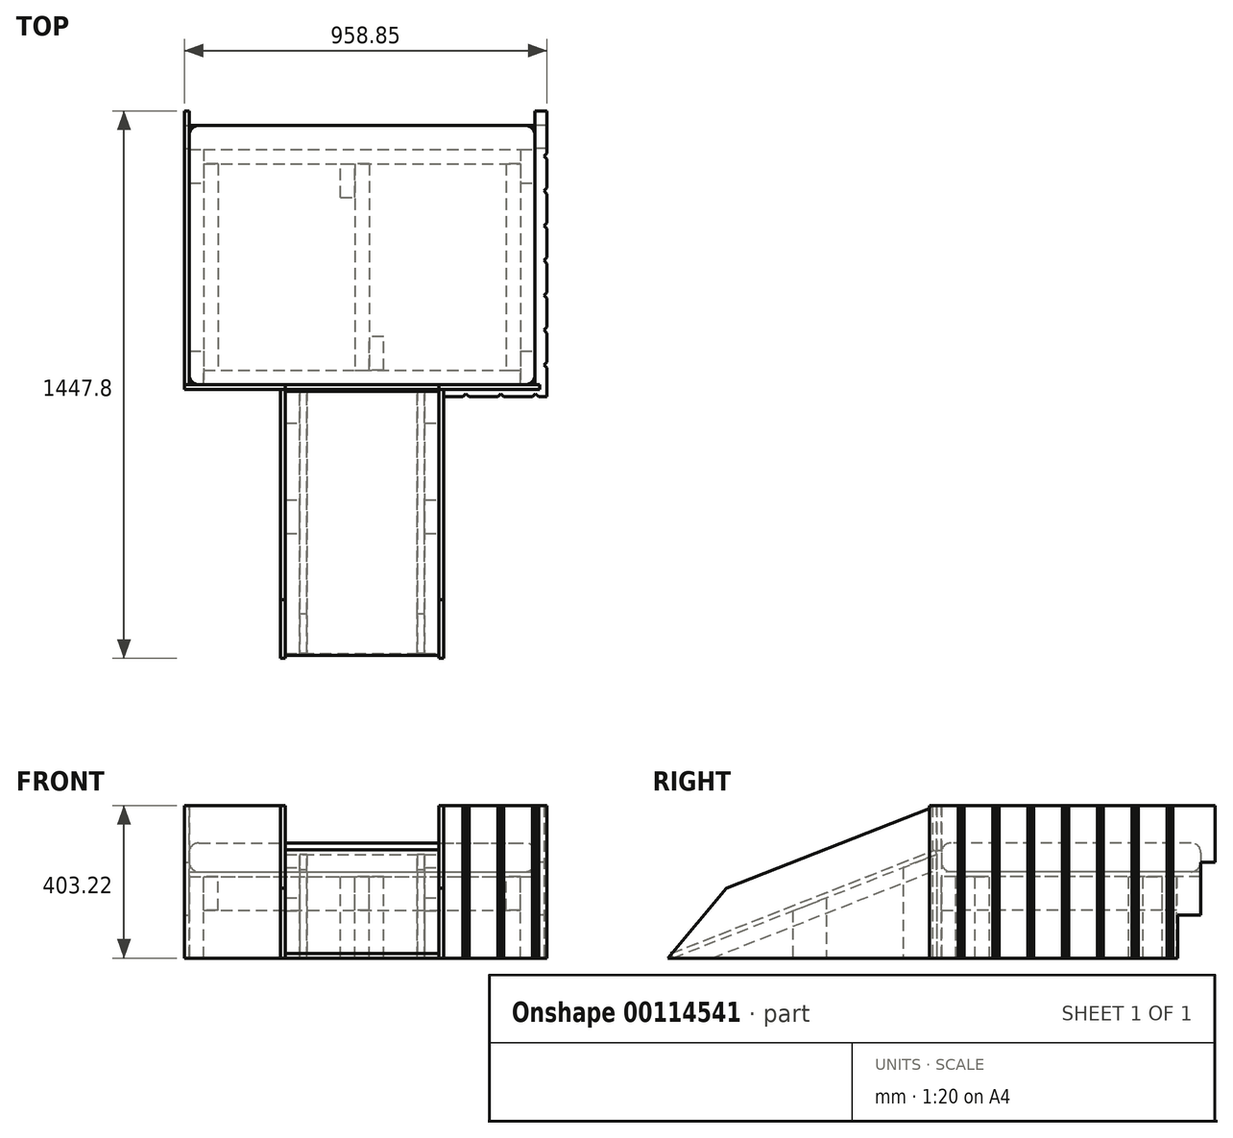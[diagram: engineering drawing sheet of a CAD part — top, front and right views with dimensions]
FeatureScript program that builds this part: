
annotation { "Feature Type Name" : "Feature", "Feature Type Description" : "" }
export const myFeature = defineFeature(function(context is Context, id is Id, definition is map)
    precondition{}
    {
        {
            var Q0;
            Q0=qCreatedBy(makeId("Top.planeOp"),FACE);
            var sketch = newSketch(context, id + "F0", { "sketchPlane" : qUnion([Q0])});
            skLineSegment(sketch, "E0.bottom", {"start": v(-457.2, 0) * mm, "end": v(457.2, 0) * mm});
            skLineSegment(sketch, "E0.top", {"start": v(-457.2, -685.8) * mm, "end": v(457.2, -685.8) * mm});
            skLineSegment(sketch, "E0.left", {"start": v(-457.2, 0) * mm, "end": v(-457.2, -685.8) * mm});
            skLineSegment(sketch, "E0.right", {"start": v(457.2, 0) * mm, "end": v(457.2, -685.8) * mm});
            skLineSegment(sketch, "E1", {"start": v(0, 0) * mm, "end": v(0, -685.8) * mm, "construction": true});
            skSolve(sketch);
        }
        {
            var Q0;
            Q0 = qSketchRegion(id + "F0", true);
            extrude(context, id + "F1", {"entities" : qUnion([Q0]), "oppositeDirection" : true, "depth" : 12.7 * mm});
        }
        {
            var Q0;
            Q0=makeQuery(id+"F1.opExtrude","CAP_FACE",FACE,{"disambiguationData":[OSD([sQuery(id+"F0.wireOp",EDGE,"E0.bottom"),sQuery(id+"F0.wireOp",EDGE,"E0.top"),sQuery(id+"F0.wireOp",EDGE,"E0.left"),sQuery(id+"F0.wireOp",EDGE,"E0.right")])],"isStart":false});
            var sketch = newSketch(context, id + "F2", { "sketchPlane" : qUnion([Q0])});
            skLineSegment(sketch, "E2.bottom", {"start": v(-457.2, 63.5) * mm, "end": v(-419.1, 63.5) * mm});
            skLineSegment(sketch, "E2.top", {"start": v(-457.2, 152.4) * mm, "end": v(-419.1, 152.4) * mm});
            skLineSegment(sketch, "E2.left", {"start": v(-457.2, 63.5) * mm, "end": v(-457.2, 152.4) * mm});
            skLineSegment(sketch, "E2.right", {"start": v(-419.1, 63.5) * mm, "end": v(-419.1, 152.4) * mm});
            skLineSegment(sketch, "E3.bottom", {"start": v(-457.2, 596.9) * mm, "end": v(-419.1, 596.9) * mm});
            skLineSegment(sketch, "E3.top", {"start": v(-457.2, 685.8) * mm, "end": v(-419.1, 685.8) * mm});
            skLineSegment(sketch, "E3.left", {"start": v(-457.2, 596.9) * mm, "end": v(-457.2, 685.8) * mm});
            skLineSegment(sketch, "E3.right", {"start": v(-419.1, 596.9) * mm, "end": v(-419.1, 685.8) * mm});
            skLineSegment(sketch, "E4.bottom", {"start": v(419.1, 63.5) * mm, "end": v(457.2, 63.5) * mm});
            skLineSegment(sketch, "E4.top", {"start": v(419.1, 152.4) * mm, "end": v(457.2, 152.4) * mm});
            skLineSegment(sketch, "E4.left", {"start": v(419.1, 63.5) * mm, "end": v(419.1, 152.4) * mm});
            skLineSegment(sketch, "E4.right", {"start": v(457.2, 63.5) * mm, "end": v(457.2, 152.4) * mm});
            skLineSegment(sketch, "E5.bottom", {"start": v(419.1, 596.9) * mm, "end": v(457.2, 596.9) * mm});
            skLineSegment(sketch, "E5.top", {"start": v(419.1, 685.8) * mm, "end": v(457.2, 685.8) * mm});
            skLineSegment(sketch, "E5.left", {"start": v(419.1, 596.9) * mm, "end": v(419.1, 685.8) * mm});
            skLineSegment(sketch, "E5.right", {"start": v(457.2, 596.9) * mm, "end": v(457.2, 685.8) * mm});
            skLineSegment(sketch, "E6.bottom", {"start": v(-57.15, 190.5) * mm, "end": v(-19.05, 190.5) * mm});
            skLineSegment(sketch, "E6.top", {"start": v(-57.15, 101.6) * mm, "end": v(-19.05, 101.6) * mm});
            skLineSegment(sketch, "E6.left", {"start": v(-57.15, 190.5) * mm, "end": v(-57.15, 101.6) * mm});
            skLineSegment(sketch, "E6.right", {"start": v(-19.05, 190.5) * mm, "end": v(-19.05, 101.6) * mm});
            skLineSegment(sketch, "E7.bottom", {"start": v(57.15, 647.7) * mm, "end": v(19.05, 647.7) * mm});
            skLineSegment(sketch, "E7.top", {"start": v(57.15, 558.8) * mm, "end": v(19.05, 558.8) * mm});
            skLineSegment(sketch, "E7.left", {"start": v(57.15, 647.7) * mm, "end": v(57.15, 558.8) * mm});
            skLineSegment(sketch, "E7.right", {"start": v(19.05, 647.7) * mm, "end": v(19.05, 558.8) * mm});
            skSolve(sketch);
        }
        {
            var Q0;
            Q0 = qSketchRegion(id + "F2", true);
            extrude(context, id + "F3", {"entities" : qUnion([Q0]), "operationType" : NewBodyOperationType.ADD, "depth" : 215.9 * mm});
        }
        {
            var Q0;
            Q0=makeQuery(id+"F3.opExtrude","CAP_FACE",FACE,{"disambiguationData":[OSD([sQuery(id+"F2.wireOp",EDGE,"E5.bottom"),sQuery(id+"F2.wireOp",EDGE,"E5.top"),sQuery(id+"F2.wireOp",EDGE,"E5.left"),sQuery(id+"F2.wireOp",EDGE,"E5.right")])],"isStart":false});
            var sketch = newSketch(context, id + "F4", { "sketchPlane" : qUnion([Q0])});
            skLineSegment(sketch, "E8.bottom", {"start": v(203.2, 698.5) * mm, "end": v(165.1, 698.5) * mm});
            skLineSegment(sketch, "E8.top", {"start": v(203.2, 787.4) * mm, "end": v(165.1, 787.4) * mm});
            skLineSegment(sketch, "E8.left", {"start": v(203.2, 698.5) * mm, "end": v(203.2, 787.4) * mm});
            skLineSegment(sketch, "E8.right", {"start": v(165.1, 698.5) * mm, "end": v(165.1, 787.4) * mm});
            skLineSegment(sketch, "E9.bottom", {"start": v(-165.1, 698.5) * mm, "end": v(-203.2, 698.5) * mm});
            skLineSegment(sketch, "E9.top", {"start": v(-165.1, 787.4) * mm, "end": v(-203.2, 787.4) * mm});
            skLineSegment(sketch, "E9.left", {"start": v(-165.1, 698.5) * mm, "end": v(-165.1, 787.4) * mm});
            skLineSegment(sketch, "E9.right", {"start": v(-203.2, 698.5) * mm, "end": v(-203.2, 787.4) * mm});
            skLineSegment(sketch, "E10.bottom", {"start": v(203.2, 990.6) * mm, "end": v(165.1, 990.6) * mm});
            skLineSegment(sketch, "E10.top", {"start": v(203.2, 1079.5) * mm, "end": v(165.1, 1079.5) * mm});
            skLineSegment(sketch, "E10.left", {"start": v(203.2, 990.6) * mm, "end": v(203.2, 1079.5) * mm});
            skLineSegment(sketch, "E10.right", {"start": v(165.1, 990.6) * mm, "end": v(165.1, 1079.5) * mm});
            skLineSegment(sketch, "E11.bottom", {"start": v(-165.1, 990.6) * mm, "end": v(-203.2, 990.6) * mm});
            skLineSegment(sketch, "E11.top", {"start": v(-165.1, 1079.5) * mm, "end": v(-203.2, 1079.5) * mm});
            skLineSegment(sketch, "E11.left", {"start": v(-165.1, 990.6) * mm, "end": v(-165.1, 1079.5) * mm});
            skLineSegment(sketch, "E11.right", {"start": v(-203.2, 990.6) * mm, "end": v(-203.2, 1079.5) * mm});
            skSolve(sketch);
        }
        {
            var Q0;
            Q0 = qSketchRegion(id + "F4", true);
            extrude(context, id + "F5", {"entities" : qUnion([Q0]), "operationType" : NewBodyOperationType.ADD, "oppositeDirection" : true, "depth" : 279.4 * mm});
        }
        {
            var Q0;
            Q0=makeQuery(id+"F5.opExtrude","SWEPT_FACE",FACE,{"disambiguationData":[OSD([sQuery(id+"F4.wireOp",EDGE,"E9.right")])]});
            var sketch = newSketch(context, id + "F6", { "sketchPlane" : qUnion([Q0])});
            skLineSegment(sketch, "E12", {"start": v(685.8, 50.8) * mm, "end": v(1397, -228.6) * mm});
            skLineSegment(sketch, "E13", {"start": v(1397, -228.6) * mm, "end": v(1397, 149.23) * mm});
            skLineSegment(sketch, "E14", {"start": v(1397, 149.23) * mm, "end": v(685.8, 149.23) * mm});
            skLineSegment(sketch, "E15", {"start": v(685.8, 149.23) * mm, "end": v(685.8, 50.8) * mm});
            skSolve(sketch);
        }
        {
            var Q0;
            Q0 = qSketchRegion(id + "F6", true);
            extrude(context, id + "F7", {"entities" : qUnion([Q0]), "operationType" : NewBodyOperationType.REMOVE, "oppositeDirection" : true, "depth" : 914.4 * mm});
        }
        {
            var Q0;
            Q0=makeQuery(id+"F7.boolean.opBoolean","COPY",FACE,{"disambiguationData":[OD(3.0)],"derivedFrom":makeQuery(id+"F7.opExtrude","SWEPT_FACE",FACE,{"disambiguationData":[OSD([sQuery(id+"F6.wireOp",EDGE,"E12")])]})});
            var sketch = newSketch(context, id + "F8", { "sketchPlane" : qUnion([Q0])});
            skLineSegment(sketch, "E16.bottom", {"start": v(-203.2, -1383.85) * mm, "end": v(203.2, -1383.85) * mm});
            skLineSegment(sketch, "E16.top", {"start": v(-203.2, -633.38) * mm, "end": v(203.2, -633.38) * mm});
            skLineSegment(sketch, "E16.left", {"start": v(-203.2, -1383.85) * mm, "end": v(-203.2, -633.38) * mm});
            skLineSegment(sketch, "E16.right", {"start": v(203.2, -1383.85) * mm, "end": v(203.2, -633.38) * mm});
            skSolve(sketch);
        }
        {
            var Q0;
            Q0 = qSketchRegion(id + "F8", true);
            extrude(context, id + "F9", {"entities" : qUnion([Q0]), "depth" : 12.7 * mm});
        }
        {
            var Q0;
            Q0=makeQuery(id+"F3.boolean.opBoolean","MERGE",FACE,{"derivedFrom":[makeQuery(id+"F1.opExtrude","SWEPT_FACE",FACE,{"disambiguationData":[OSD([sQuery(id+"F0.wireOp",EDGE,"E0.top")])]}),makeQuery(id+"F3.opExtrude","SWEPT_FACE",FACE,{"disambiguationData":[OSD([sQuery(id+"F2.wireOp",EDGE,"E3.top")])]}),makeQuery(id+"F3.opExtrude","SWEPT_FACE",FACE,{"disambiguationData":[OSD([sQuery(id+"F2.wireOp",EDGE,"E5.top")])]})]});
            var sketch = newSketch(context, id + "F10", { "sketchPlane" : qUnion([Q0])});
            skLineSegment(sketch, "E17", {"start": v(469.9, -228.6) * mm, "end": v(-469.9, -228.6) * mm});
            skLineSegment(sketch, "E18", {"start": v(-469.9, -228.6) * mm, "end": v(-469.9, 174.62) * mm});
            skLineSegment(sketch, "E19", {"start": v(-469.9, 174.62) * mm, "end": v(-203.2, 174.62) * mm});
            skLineSegment(sketch, "E20", {"start": v(-203.2, 174.62) * mm, "end": v(-203.2, 57.15) * mm});
            skLineSegment(sketch, "E21", {"start": v(-203.2, 57.15) * mm, "end": v(203.2, 57.15) * mm});
            skLineSegment(sketch, "E22", {"start": v(203.2, 57.15) * mm, "end": v(203.2, 174.63) * mm});
            skLineSegment(sketch, "E23", {"start": v(203.2, 174.63) * mm, "end": v(469.9, 174.63) * mm});
            skLineSegment(sketch, "E24", {"start": v(469.9, 174.63) * mm, "end": v(469.9, -228.6) * mm});
            skSolve(sketch);
        }
        {
            var Q0;
            Q0 = qSketchRegion(id + "F10", true);
            extrude(context, id + "F11", {"entities" : qUnion([Q0]), "depth" : 12.7 * mm});
        }
        {
            var Q0;
            Q0=makeQuery(id+"F3.boolean.opBoolean","MERGE",FACE,{"derivedFrom":[makeQuery(id+"F1.opExtrude","SWEPT_FACE",FACE,{"disambiguationData":[OSD([sQuery(id+"F0.wireOp",EDGE,"E0.right")])]}),makeQuery(id+"F3.opExtrude","SWEPT_FACE",FACE,{"disambiguationData":[OSD([sQuery(id+"F2.wireOp",EDGE,"E4.right")])]}),makeQuery(id+"F3.opExtrude","SWEPT_FACE",FACE,{"disambiguationData":[OSD([sQuery(id+"F2.wireOp",EDGE,"E5.right")])]})]});
            var sketch = newSketch(context, id + "F12", { "sketchPlane" : qUnion([Q0])});
            skLineSegment(sketch, "E25", {"start": v(-685.8, -228.6) * mm, "end": v(-685.8, 174.62) * mm});
            skLineSegment(sketch, "E26", {"start": v(-685.8, 174.63) * mm, "end": v(38.1, 174.63) * mm});
            skLineSegment(sketch, "E27", {"start": v(-60.32, -228.6) * mm, "end": v(-685.8, -228.6) * mm});
            skLineSegment(sketch, "E28", {"start": v(38.1, 174.63) * mm, "end": v(38.1, 25.4) * mm});
            skLineSegment(sketch, "E29", {"start": v(38.1, 25.4) * mm, "end": v(0, 25.4) * mm});
            skLineSegment(sketch, "E30", {"start": v(0, 25.4) * mm, "end": v(0, -114.3) * mm});
            skLineSegment(sketch, "E31", {"start": v(0, -114.3) * mm, "end": v(-60.32, -114.3) * mm});
            skLineSegment(sketch, "E32", {"start": v(-60.32, -228.6) * mm, "end": v(-60.32, -114.3) * mm});
            skSolve(sketch);
        }
        {
            var Q0;
            Q0 = qSketchRegion(id + "F12", true);
            extrude(context, id + "F13", {"entities" : qUnion([Q0]), "depth" : 12.7 * mm});
        }
        {
            var Q0;
            Q0=makeQuery(id+"F3.boolean.opBoolean","MERGE",FACE,{"derivedFrom":[makeQuery(id+"F1.opExtrude","SWEPT_FACE",FACE,{"disambiguationData":[OSD([sQuery(id+"F0.wireOp",EDGE,"E0.left")])]}),makeQuery(id+"F3.opExtrude","SWEPT_FACE",FACE,{"disambiguationData":[OSD([sQuery(id+"F2.wireOp",EDGE,"E2.left")])]}),makeQuery(id+"F3.opExtrude","SWEPT_FACE",FACE,{"disambiguationData":[OSD([sQuery(id+"F2.wireOp",EDGE,"E3.left")])]})]});
            var sketch = newSketch(context, id + "F14", { "sketchPlane" : qUnion([Q0])});
            skLineSegment(sketch, "E33", {"start": v(685.8, -228.6) * mm, "end": v(60.32, -228.6) * mm});
            skLineSegment(sketch, "E34", {"start": v(-38.1, 174.62) * mm, "end": v(685.8, 174.63) * mm});
            skLineSegment(sketch, "E35", {"start": v(685.8, 174.63) * mm, "end": v(685.8, -228.6) * mm});
            skLineSegment(sketch, "E36", {"start": v(60.32, -228.6) * mm, "end": v(60.32, -114.3) * mm});
            skLineSegment(sketch, "E37", {"start": v(60.32, -114.3) * mm, "end": v(0, -114.3) * mm});
            skLineSegment(sketch, "E38", {"start": v(0, -114.3) * mm, "end": v(0, 25.4) * mm});
            skLineSegment(sketch, "E39", {"start": v(0, 25.4) * mm, "end": v(-38.1, 25.4) * mm});
            skLineSegment(sketch, "E40", {"start": v(-38.1, 25.4) * mm, "end": v(-38.1, 174.62) * mm});
            skSolve(sketch);
        }
        {
            var Q0;
            Q0 = qSketchRegion(id + "F14", true);
            extrude(context, id + "F15", {"entities" : qUnion([Q0]), "depth" : 12.7 * mm});
        }
        {
            var Q0;
            Q0=makeQuery(id+"F5.opExtrude","SWEPT_FACE",FACE,{"disambiguationData":[OSD([sQuery(id+"F4.wireOp",EDGE,"E8.left")])]});
            var sketch = newSketch(context, id + "F16", { "sketchPlane" : qUnion([Q0])});
            skLineSegment(sketch, "E41", {"start": v(-698.5, -228.6) * mm, "end": v(-698.5, 174.63) * mm});
            skLineSegment(sketch, "E42", {"start": v(-698.5, 174.63) * mm, "end": v(-1254.7, -43.88) * mm});
            skLineSegment(sketch, "E43", {"start": v(-1409.7, -228.6) * mm, "end": v(-698.5, -228.6) * mm});
            skLineSegment(sketch, "E44", {"start": v(-1409.7, -228.6) * mm, "end": v(-1254.7, -43.88) * mm});
            skSolve(sketch);
        }
        {
            var Q0;
            Q0 = qSketchRegion(id + "F16", true);
            extrude(context, id + "F17", {"entities" : qUnion([Q0]), "depth" : 12.7 * mm});
        }
        {
            var Q0;
            Q0=makeQuery(id+"F3.opExtrude","SWEPT_FACE",FACE,{"disambiguationData":[OSD([sQuery(id+"F2.wireOp",EDGE,"E5.left")])]});
            var sketch = newSketch(context, id + "F18", { "sketchPlane" : qUnion([Q0])});
            skLineSegment(sketch, "E45.bottom", {"start": v(685.8, -12.7) * mm, "end": v(647.7, -12.7) * mm});
            skLineSegment(sketch, "E45.top", {"start": v(685.8, -101.6) * mm, "end": v(647.7, -101.6) * mm});
            skLineSegment(sketch, "E45.left", {"start": v(685.8, -12.7) * mm, "end": v(685.8, -101.6) * mm});
            skLineSegment(sketch, "E45.right", {"start": v(647.7, -12.7) * mm, "end": v(647.7, -101.6) * mm});
            skLineSegment(sketch, "E46.bottom", {"start": v(63.5, -12.7) * mm, "end": v(101.6, -12.7) * mm});
            skLineSegment(sketch, "E46.top", {"start": v(63.5, -101.6) * mm, "end": v(101.6, -101.6) * mm});
            skLineSegment(sketch, "E46.left", {"start": v(63.5, -12.7) * mm, "end": v(63.5, -101.6) * mm});
            skLineSegment(sketch, "E46.right", {"start": v(101.6, -12.7) * mm, "end": v(101.6, -101.6) * mm});
            skSolve(sketch);
        }
        {
            var Q0;
            Q0 = qSketchRegion(id + "F18", true);
            extrude(context, id + "F19", {"entities" : qUnion([Q0]), "depth" : 838.2 * mm});
        }
        {
            var Q0;
            Q0=makeQuery(id+"F19.opExtrude","SWEPT_FACE",FACE,{"disambiguationData":[OSD([sQuery(id+"F18.wireOp",EDGE,"E45.right")])]});
            var sketch = newSketch(context, id + "F20", { "sketchPlane" : qUnion([Q0])});
            skLineSegment(sketch, "E47.bottom", {"start": v(-19.05, -12.7) * mm, "end": v(19.05, -12.7) * mm});
            skLineSegment(sketch, "E47.top", {"start": v(-19.05, -101.6) * mm, "end": v(19.05, -101.6) * mm});
            skLineSegment(sketch, "E47.left", {"start": v(-19.05, -12.7) * mm, "end": v(-19.05, -101.6) * mm});
            skLineSegment(sketch, "E47.right", {"start": v(19.05, -12.7) * mm, "end": v(19.05, -101.6) * mm});
            skLineSegment(sketch, "E48.bottom", {"start": v(-419.1, -12.7) * mm, "end": v(-381, -12.7) * mm});
            skLineSegment(sketch, "E48.top", {"start": v(-419.1, -101.6) * mm, "end": v(-381, -101.6) * mm});
            skLineSegment(sketch, "E48.left", {"start": v(-419.1, -12.7) * mm, "end": v(-419.1, -101.6) * mm});
            skLineSegment(sketch, "E48.right", {"start": v(-381, -12.7) * mm, "end": v(-381, -101.6) * mm});
            skLineSegment(sketch, "E49.bottom", {"start": v(419.1, -12.7) * mm, "end": v(381, -12.7) * mm});
            skLineSegment(sketch, "E49.top", {"start": v(419.1, -101.6) * mm, "end": v(381, -101.6) * mm});
            skLineSegment(sketch, "E49.left", {"start": v(419.1, -12.7) * mm, "end": v(419.1, -101.6) * mm});
            skLineSegment(sketch, "E49.right", {"start": v(381, -12.7) * mm, "end": v(381, -101.6) * mm});
            skSolve(sketch);
        }
        {
            var Q0;
            Q0 = qSketchRegion(id + "F20", true);
            extrude(context, id + "F21", {"entities" : qUnion([Q0]), "endBound" : BoundingType.UP_TO_NEXT, "depth" : 25.4 * mm});
        }
        {
            var Q0;
            Q0=makeQuery(id+"F17.opExtrude","SWEPT_BODY",BODY,{"disambiguationData":[OSD([sQuery(id+"F16.wireOp",EDGE,"E41"),sQuery(id+"F16.wireOp",EDGE,"fiiTlYLV-duia-QpJI-SALt-FYDScrY8uBnS"),sQuery(id+"F16.wireOp",EDGE,"e7RRUxPj-3naJ-ncjy-4rKp-VtwRg2sKKchD"),sQuery(id+"F16.wireOp",EDGE,"E42"),sQuery(id+"F16.wireOp",EDGE,"E43"),sQuery(id+"F16.wireOp",EDGE,"E44")])]});
            transform(context, id + "F22", {"entities" : qUnion([Q0]), "transformType" : TransformType.TRANSLATION_3D, "dx" : -419.1 * mm, "dy" : 0 * mm, "dz" : 0 * mm, "makeCopy" : true});
        }
        {
            var Q0;
            Q0=makeQuery(id+"F5.opExtrude","SWEPT_FACE",FACE,{"disambiguationData":[OSD([sQuery(id+"F4.wireOp",EDGE,"E11.left")])]});
            var sketch = newSketch(context, id + "F23", { "sketchPlane" : qUnion([Q0])});
            skLineSegment(sketch, "E50", {"start": v(-698.5, 45.81) * mm, "end": v(-1397, -228.6) * mm});
            skLineSegment(sketch, "E51", {"start": v(-1397, -228.6) * mm, "end": v(-1292.8, -228.6) * mm});
            skLineSegment(sketch, "E52", {"start": v(-1292.8, -228.6) * mm, "end": v(-698.5, 4.88) * mm});
            skLineSegment(sketch, "E53", {"start": v(-698.5, 4.88) * mm, "end": v(-698.5, 45.81) * mm});
            skSolve(sketch);
        }
        {
            var Q0;
            Q0 = qSketchRegion(id + "F23", true);
            extrude(context, id + "F24", {"entities" : qUnion([Q0]), "depth" : 19.05 * mm});
        }
        {
            var Q0;
            Q0=makeQuery(id+"F24.opExtrude","SWEPT_BODY",BODY,{"disambiguationData":[OSD([sQuery(id+"F23.wireOp",EDGE,"E50"),sQuery(id+"F23.wireOp",EDGE,"E51"),sQuery(id+"F23.wireOp",EDGE,"E52"),sQuery(id+"F23.wireOp",EDGE,"E53")])]});
            transform(context, id + "F25", {"entities" : qUnion([Q0]), "transformType" : TransformType.TRANSLATION_3D, "dx" : 311.15 * mm, "dy" : 0 * mm, "dz" : 0 * mm, "makeCopy" : true});
        }
        {
            var Q0;
            Q0=makeQuery(id+"F11.opExtrude","SWEPT_FACE",FACE,{"disambiguationData":[OSD([sQuery(id+"F10.wireOp",EDGE,"E17")])]});
            var sketch = newSketch(context, id + "F26", { "sketchPlane" : qUnion([Q0])});
            skLineSegment(sketch, "E54", {"start": v(215.9, 698.5) * mm, "end": v(215.9, 717.55) * mm});
            skLineSegment(sketch, "E55", {"start": v(215.9, 717.55) * mm, "end": v(266.7, 717.55) * mm});
            skLineSegment(sketch, "E56", {"start": v(266.7, 717.55) * mm, "end": v(274.64, 709.61) * mm});
            skLineSegment(sketch, "E57", {"start": v(274.64, 709.61) * mm, "end": v(282.57, 717.55) * mm});
            skLineSegment(sketch, "E58", {"start": v(282.57, 717.55) * mm, "end": v(358.77, 717.55) * mm});
            skLineSegment(sketch, "E59", {"start": v(358.77, 717.55) * mm, "end": v(366.71, 709.61) * mm});
            skLineSegment(sketch, "E60", {"start": v(366.71, 709.61) * mm, "end": v(374.65, 717.55) * mm});
            skLineSegment(sketch, "E61", {"start": v(374.65, 717.55) * mm, "end": v(450.85, 717.55) * mm});
            skLineSegment(sketch, "E62", {"start": v(450.85, 717.55) * mm, "end": v(458.79, 709.61) * mm});
            skLineSegment(sketch, "E63", {"start": v(458.79, 709.61) * mm, "end": v(466.72, 717.55) * mm});
            skLineSegment(sketch, "E64", {"start": v(466.72, 717.55) * mm, "end": v(488.95, 717.55) * mm});
            skLineSegment(sketch, "E65", {"start": v(488.95, 717.55) * mm, "end": v(488.95, 641.35) * mm});
            skLineSegment(sketch, "E66", {"start": v(488.95, 641.35) * mm, "end": v(481.01, 633.41) * mm});
            skLineSegment(sketch, "E67", {"start": v(481.01, 633.41) * mm, "end": v(488.95, 625.48) * mm});
            skLineSegment(sketch, "E68", {"start": v(488.95, 625.48) * mm, "end": v(488.95, 549.28) * mm});
            skLineSegment(sketch, "E69", {"start": v(488.95, 549.28) * mm, "end": v(481.01, 541.34) * mm});
            skLineSegment(sketch, "E70", {"start": v(481.01, 541.34) * mm, "end": v(488.95, 533.4) * mm});
            skLineSegment(sketch, "E71", {"start": v(488.95, 533.4) * mm, "end": v(488.95, 457.2) * mm});
            skLineSegment(sketch, "E72", {"start": v(488.95, 457.2) * mm, "end": v(481.01, 449.26) * mm});
            skLineSegment(sketch, "E73", {"start": v(481.01, 449.26) * mm, "end": v(488.95, 441.33) * mm});
            skLineSegment(sketch, "E74", {"start": v(488.95, 441.33) * mm, "end": v(488.95, 365.13) * mm});
            skLineSegment(sketch, "E75", {"start": v(488.95, 365.13) * mm, "end": v(481.01, 357.19) * mm});
            skLineSegment(sketch, "E76", {"start": v(481.01, 357.19) * mm, "end": v(488.95, 349.25) * mm});
            skLineSegment(sketch, "E77", {"start": v(488.95, 349.25) * mm, "end": v(488.95, 273.05) * mm});
            skLineSegment(sketch, "E78", {"start": v(469.9, 698.5) * mm, "end": v(215.9, 698.5) * mm});
            skLineSegment(sketch, "E79", {"start": v(469.9, 698.5) * mm, "end": v(469.9, 60.32) * mm});
            skLineSegment(sketch, "E80", {"start": v(469.9, 60.32) * mm, "end": v(488.95, 60.32) * mm});
            skLineSegment(sketch, "E81", {"start": v(488.95, 273.05) * mm, "end": v(481.01, 265.11) * mm});
            skLineSegment(sketch, "E82", {"start": v(481.01, 265.11) * mm, "end": v(488.95, 257.18) * mm});
            skLineSegment(sketch, "E83", {"start": v(488.95, 180.98) * mm, "end": v(481.01, 173.04) * mm});
            skLineSegment(sketch, "E84", {"start": v(481.01, 173.04) * mm, "end": v(488.95, 165.1) * mm});
            skLineSegment(sketch, "E85", {"start": v(488.95, 88.9) * mm, "end": v(481.01, 80.96) * mm});
            skLineSegment(sketch, "E86", {"start": v(481.01, 80.96) * mm, "end": v(488.95, 73.03) * mm});
            skLineSegment(sketch, "E87.trimOffspring", {"start": v(488.95, 257.18) * mm, "end": v(488.95, 180.98) * mm});
            skLineSegment(sketch, "E88.trimOffspring", {"start": v(488.95, 165.1) * mm, "end": v(488.95, 88.9) * mm});
            skLineSegment(sketch, "E89.trimOffspring", {"start": v(488.95, 73.03) * mm, "end": v(488.95, 60.32) * mm});
            skSolve(sketch);
        }
        {
            var Q0;
            Q0 = qSketchRegion(id + "F26", true);
            var Q1;
            Q1=makeQuery(id+"F13.opExtrude","SWEPT_FACE",FACE,{"disambiguationData":[OSD([sQuery(id+"F12.wireOp",EDGE,"E26")])]});
            extrude(context, id + "F27", {"entities" : qUnion([Q0]), "endBound" : BoundingType.UP_TO_SURFACE, "oppositeDirection" : true, "endBoundEntityFace" : qUnion([Q1]), "depth" : 495.3 * mm});
        }
        {
            var Q0;
            Q0=makeQuery(id+"F1.opExtrude","CAP_FACE",FACE,{"disambiguationData":[OSD([sQuery(id+"F0.wireOp",EDGE,"E0.bottom"),sQuery(id+"F0.wireOp",EDGE,"E0.top"),sQuery(id+"F0.wireOp",EDGE,"E0.left"),sQuery(id+"F0.wireOp",EDGE,"E0.right")])],"isStart":true});
            var sketch = newSketch(context, id + "F28", { "sketchPlane" : qUnion([Q0])});
            skLineSegment(sketch, "E90.bottom", {"start": v(-457.2, -685.8) * mm, "end": v(457.2, -685.8) * mm});
            skLineSegment(sketch, "E90.top", {"start": v(-457.2, 0) * mm, "end": v(457.2, 0) * mm});
            skLineSegment(sketch, "E90.left", {"start": v(-457.2, -685.8) * mm, "end": v(-457.2, 0) * mm});
            skLineSegment(sketch, "E90.right", {"start": v(457.2, -685.8) * mm, "end": v(457.2, 0) * mm});
            skSolve(sketch);
        }
        {
            var Q0;
            Q0 = qSketchRegion(id + "F28", true);
            extrude(context, id + "F29", {"entities" : qUnion([Q0]), "depth" : 76.2 * mm});
        }
        {
            var Q0;
            Q0=makeQuery(id+"F29.opExtrude","CAP_FACE",FACE,{"disambiguationData":[OSD([sQuery(id+"F28.wireOp",EDGE,"E90.bottom"),sQuery(id+"F28.wireOp",EDGE,"E90.top"),sQuery(id+"F28.wireOp",EDGE,"E90.left"),sQuery(id+"F28.wireOp",EDGE,"E90.right")])],"isStart":false});
            var Q1;
            Q1=makeQuery(id+"F29.opExtrude","SWEPT_FACE",FACE,{"disambiguationData":[OSD([sQuery(id+"F28.wireOp",EDGE,"E90.top")])]});
            var Q2;
            Q2=makeQuery(id+"F29.opExtrude","SWEPT_FACE",FACE,{"disambiguationData":[OSD([sQuery(id+"F28.wireOp",EDGE,"E90.right")])]});
            var Q3;
            Q3=makeQuery(id+"F29.opExtrude","SWEPT_FACE",FACE,{"disambiguationData":[OSD([sQuery(id+"F28.wireOp",EDGE,"E90.bottom")])]});
            var Q4;
            Q4=makeQuery(id+"F29.opExtrude","SWEPT_FACE",FACE,{"disambiguationData":[OSD([sQuery(id+"F28.wireOp",EDGE,"E90.left")])]});
            fillet(context, id + "F30", {"entities" : qUnion([Q0, Q1, Q2, Q3, Q4]), "radius" : 25.4 * mm, "tangentPropagation" : true, "allowEdgeOverflow" : false});
        }
        {
            var Q0;
            Q0=makeQuery(id+"F13.opExtrude","CAP_FACE",FACE,{"disambiguationData":[OSD([sQuery(id+"F12.wireOp",EDGE,"E25"),sQuery(id+"F12.wireOp",EDGE,"E26"),sQuery(id+"F12.wireOp",EDGE,"E27"),sQuery(id+"F12.wireOp",EDGE,"E28"),sQuery(id+"F12.wireOp",EDGE,"E29"),sQuery(id+"F12.wireOp",EDGE,"E30"),sQuery(id+"F12.wireOp",EDGE,"E31"),sQuery(id+"F12.wireOp",EDGE,"E32")])],"isStart":false});
            var sketch = newSketch(context, id + "F31", { "sketchPlane" : qUnion([Q0])});
            skLineSegment(sketch, "E91", {"start": v(38.1, 174.63) * mm, "end": v(38.1, 25.4) * mm});
            skLineSegment(sketch, "E92", {"start": v(38.1, 25.4) * mm, "end": v(0, 25.4) * mm});
            skLineSegment(sketch, "E93", {"start": v(0, 25.4) * mm, "end": v(0, -114.3) * mm});
            skLineSegment(sketch, "E94", {"start": v(0, -114.3) * mm, "end": v(-60.32, -114.3) * mm});
            skLineSegment(sketch, "E95", {"start": v(-60.32, -114.3) * mm, "end": v(-60.32, 174.63) * mm});
            skLineSegment(sketch, "E96", {"start": v(-60.32, 174.63) * mm, "end": v(38.1, 174.63) * mm});
            skSolve(sketch);
        }
        {
            var Q0;
            Q0 = qSketchRegion(id + "F31", true);
            extrude(context, id + "F32", {"entities" : qUnion([Q0]), "operationType" : NewBodyOperationType.ADD, "depth" : 19.05 * mm});
        }
    });
